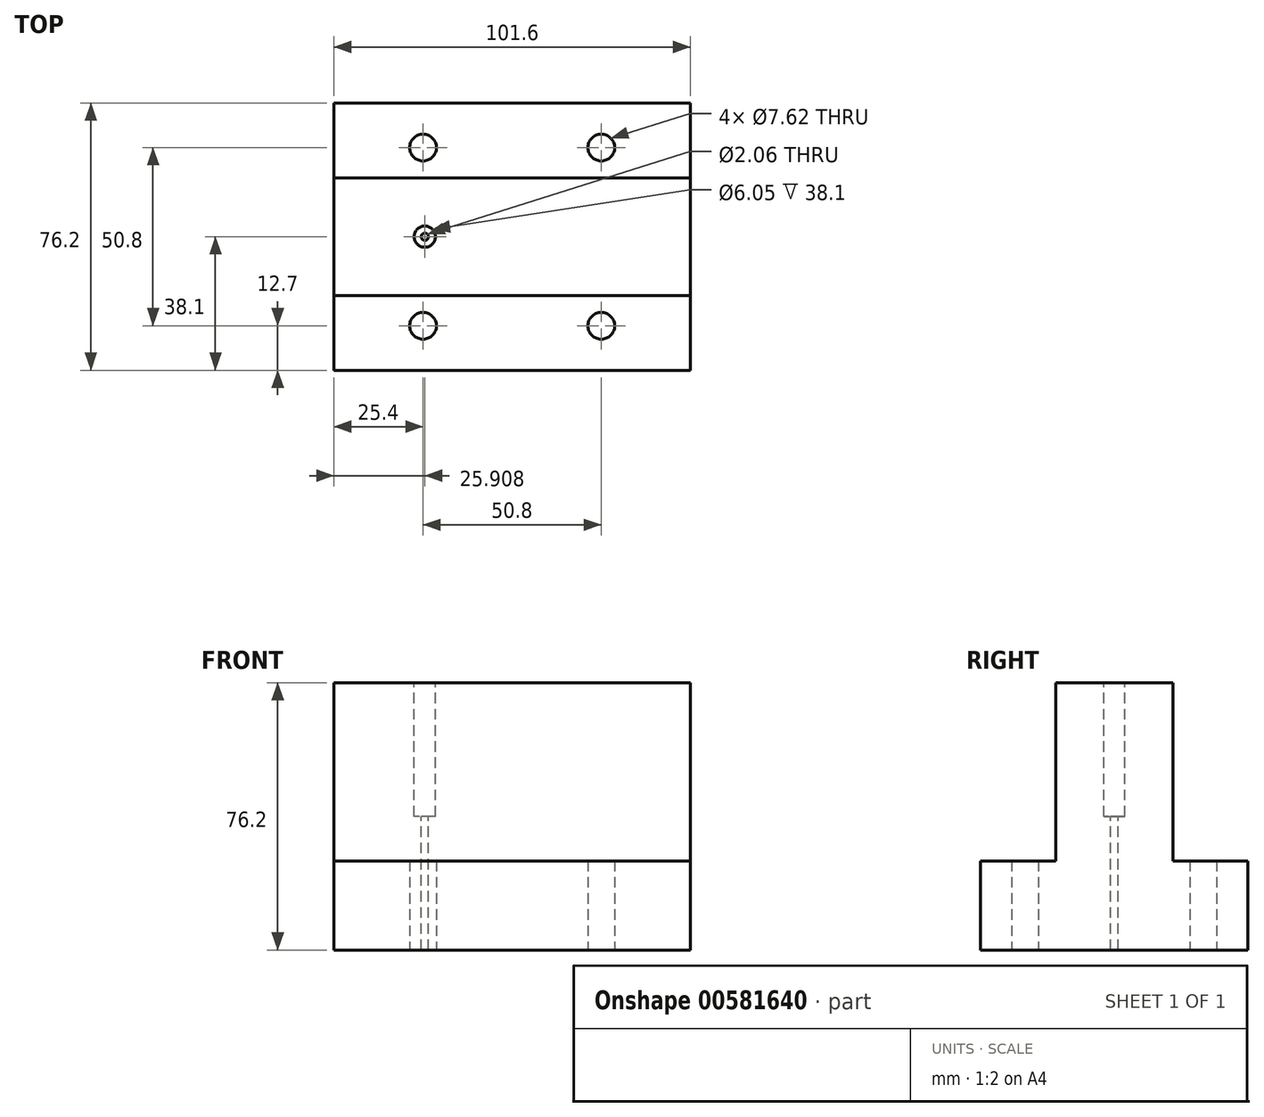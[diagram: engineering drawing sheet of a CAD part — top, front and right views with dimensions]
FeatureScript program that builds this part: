
annotation { "Feature Type Name" : "Feature", "Feature Type Description" : "" }
export const myFeature = defineFeature(function(context is Context, id is Id, definition is map)
    precondition{}
    {
        {
            var Q0;
            Q0=qCreatedBy(makeId("Top.planeOp"),FACE);
            var sketch = newSketch(context, id + "F0", { "sketchPlane" : qUnion([Q0])});
            skLineSegment(sketch, "E0.bottom", {"start": v(50.8, -38.1) * mm, "end": v(-50.8, -38.1) * mm});
            skLineSegment(sketch, "E0.top", {"start": v(50.8, 38.1) * mm, "end": v(-50.8, 38.1) * mm});
            skLineSegment(sketch, "E0.left", {"start": v(50.8, -38.1) * mm, "end": v(50.8, 38.1) * mm});
            skLineSegment(sketch, "E0.right", {"start": v(-50.8, -38.1) * mm, "end": v(-50.8, 38.1) * mm});
            skPoint(sketch, "E0.middle", {"position": v(0, 0) * mm});
            skLineSegment(sketch, "E1.bottom", {"start": v(-25.4, 25.4) * mm, "end": v(25.4, 25.4) * mm});
            skLineSegment(sketch, "E1.top", {"start": v(-25.4, -25.4) * mm, "end": v(25.4, -25.4) * mm});
            skLineSegment(sketch, "E1.left", {"start": v(-25.4, 25.4) * mm, "end": v(-25.4, -25.4) * mm});
            skLineSegment(sketch, "E1.right", {"start": v(25.4, 25.4) * mm, "end": v(25.4, -25.4) * mm});
            skCircle(sketch, "E2", {"center": v(25.4, 25.4) * mm, "radius": 3.81 * mm});
            skCircle(sketch, "E3", {"center": v(-25.4, 25.4) * mm, "radius": 3.81 * mm});
            skCircle(sketch, "E4", {"center": v(-25.4, -25.4) * mm, "radius": 3.81 * mm});
            skCircle(sketch, "E5", {"center": v(25.4, -25.4) * mm, "radius": 3.81 * mm});
            skSolve(sketch);
        }
        {
            var Q0;
            Q0=makeQuery(id+"F0.imprint","IMPRINT",FACE,{"disambiguationData":[TD([[makeQuery(id+"F0.imprint","IMPRINT",EDGE,{"derivedFrom":sQuery(id+"F0.wireOp",EDGE,"E0.bottom")}),-1.0]])]});
            var Q1;
            {var subQ5=sQuery(id+"F0.wireOp",EDGE,"E3");var subQ13=sQuery(id+"F0.wireOp",EDGE,"E1.bottom");var subQ14=makeQuery(id+"F0.imprint","INTERSECT",VERTEX,{"derivedFrom":[subQ13,subQ5]});Q1=makeQuery(id+"F0.imprint","IMPRINT",FACE,{"disambiguationData":[TD([[makeQuery(id+"F0.imprint","IMPRINT",EDGE,{"disambiguationData":[TD([[subQ14,-1.0]])],"derivedFrom":subQ13}),-1.0]])]});}
            extrude(context, id + "F1", {"entities" : qUnion([Q0, Q1]), "depth" : 25.4 * mm, "offsetDistance" : 25.4 * mm});
        }
        {
            var Q0;
            Q0=makeQuery(id+"F1.opExtrude","CAP_FACE",FACE,{"disambiguationData":[OSD([sQuery(id+"F0.wireOp",EDGE,"E0.bottom"),sQuery(id+"F0.wireOp",EDGE,"E0.top"),sQuery(id+"F0.wireOp",EDGE,"E0.left"),sQuery(id+"F0.wireOp",EDGE,"E0.right"),sQuery(id+"F0.wireOp",EDGE,"E2"),sQuery(id+"F0.wireOp",EDGE,"E3"),sQuery(id+"F0.wireOp",EDGE,"E4"),sQuery(id+"F0.wireOp",EDGE,"E5")])],"isStart":false});
            var sketch = newSketch(context, id + "F2", { "sketchPlane" : qUnion([Q0])});
            skLineSegment(sketch, "E6.bottom", {"start": v(-50.8, 16.75) * mm, "end": v(50.8, 16.75) * mm});
            skLineSegment(sketch, "E6.top", {"start": v(-50.8, -16.75) * mm, "end": v(50.8, -16.75) * mm});
            skLineSegment(sketch, "E6.left", {"start": v(-50.8, 16.75) * mm, "end": v(-50.8, -16.75) * mm});
            skLineSegment(sketch, "E6.right", {"start": v(50.8, 16.75) * mm, "end": v(50.8, -16.75) * mm});
            skPoint(sketch, "E6.middle", {"position": v(0, 0) * mm});
            skSolve(sketch);
        }
        {
            var Q0;
            Q0=makeQuery(id+"F2.imprint","IMPRINT",FACE,{"disambiguationData":[TD([[makeQuery(id+"F2.imprint","IMPRINT",EDGE,{"derivedFrom":sQuery(id+"F2.wireOp",EDGE,"E6.bottom")}),-1.0]])]});
            extrude(context, id + "F3", {"entities" : qUnion([Q0]), "operationType" : NewBodyOperationType.ADD, "depth" : 50.8 * mm, "offsetDistance" : 25.4 * mm});
        }
        {
            var Q0;
            Q0=makeQuery(id+"F3.opExtrude","CAP_FACE",FACE,{"disambiguationData":[OSD([sQuery(id+"F2.wireOp",EDGE,"E6.bottom"),sQuery(id+"F2.wireOp",EDGE,"E6.top"),sQuery(id+"F2.wireOp",EDGE,"E6.left"),sQuery(id+"F2.wireOp",EDGE,"E6.right")])],"isStart":false});
            var sketch = newSketch(context, id + "F4", { "sketchPlane" : qUnion([Q0])});
            skLineSegment(sketch, "E7", {"start": v(0, 0) * mm, "end": v(-24.9, 0) * mm});
            skCircle(sketch, "E8", {"center": v(-24.9, 0) * mm, "radius": 1.03 * mm});
            skSolve(sketch);
        }
        {
            var Q0;
            Q0=makeQuery(id+"F4.imprint","IMPRINT",FACE,{"disambiguationData":[TD([[makeQuery(id+"F4.imprint","IMPRINT",EDGE,{"derivedFrom":sQuery(id+"F4.wireOp",EDGE,"E8")}),1.0]])]});
            extrude(context, id + "F5", {"entities" : qUnion([Q0]), "operationType" : NewBodyOperationType.REMOVE, "oppositeDirection" : true, "depth" : 101.6 * mm, "offsetDistance" : 25.4 * mm});
        }
        {
            var Q0;
            Q0=makeQuery(id+"F3.opExtrude","CAP_FACE",FACE,{"disambiguationData":[OSD([sQuery(id+"F2.wireOp",EDGE,"E6.bottom"),sQuery(id+"F2.wireOp",EDGE,"E6.top"),sQuery(id+"F2.wireOp",EDGE,"E6.left"),sQuery(id+"F2.wireOp",EDGE,"E6.right")])],"isStart":false});
            var sketch = newSketch(context, id + "F6", { "sketchPlane" : qUnion([Q0])});
            skCircle(sketch, "E9", {"center": v(-24.9, 0) * mm, "radius": 3.02 * mm});
            skSolve(sketch);
        }
        {
            var Q0;
            Q0=makeQuery(id+"F6.imprint","IMPRINT",FACE,{"disambiguationData":[TD([[makeQuery(id+"F6.imprint","IMPRINT",EDGE,{"derivedFrom":sQuery(id+"F6.wireOp",EDGE,"E9")}),1.0]])]});
            extrude(context, id + "F7", {"entities" : qUnion([Q0]), "operationType" : NewBodyOperationType.REMOVE, "oppositeDirection" : true, "depth" : 38.1 * mm, "offsetDistance" : 25.4 * mm});
        }
    });
